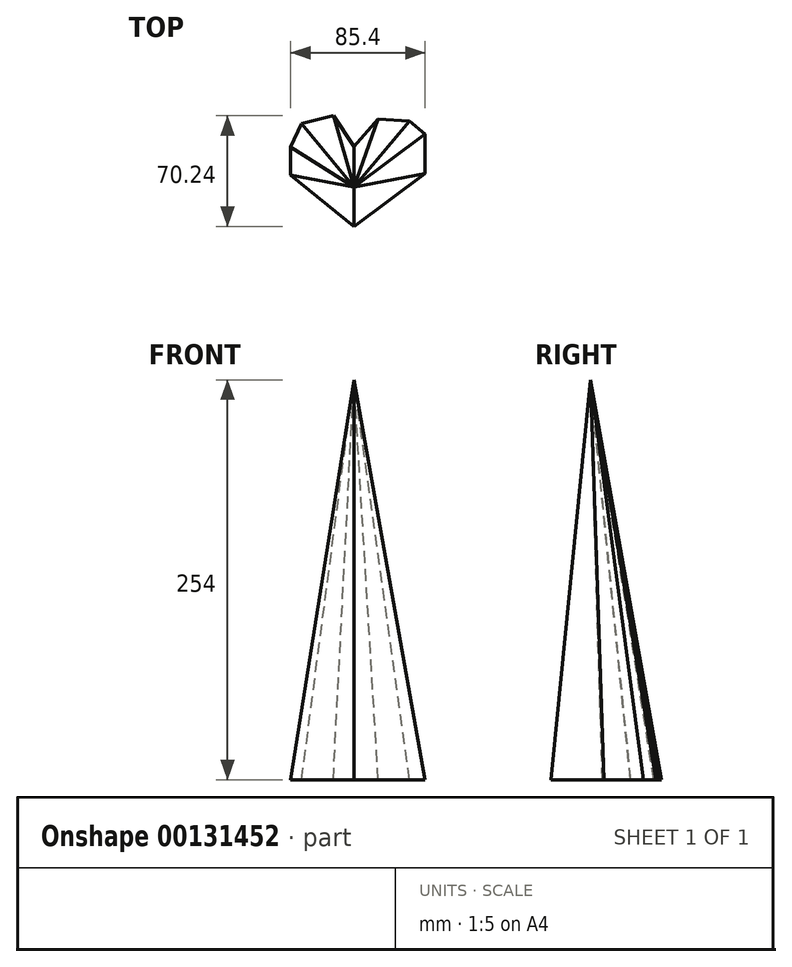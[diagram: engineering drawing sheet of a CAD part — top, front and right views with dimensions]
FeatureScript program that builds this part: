
annotation { "Feature Type Name" : "Feature", "Feature Type Description" : "" }
export const myFeature = defineFeature(function(context is Context, id is Id, definition is map)
    precondition{}
    {
        {
            var Q0;
            Q0=qCreatedBy(makeId("Top.planeOp"),FACE);
            var sketch = newSketch(context, id + "F0", { "sketchPlane" : qUnion([Q0])});
            skLineSegment(sketch, "E0", {"start": v(0, 25.8) * mm, "end": v(15.45, 43.28) * mm});
            skLineSegment(sketch, "E1", {"start": v(15.45, 43.28) * mm, "end": v(35.27, 41.83) * mm});
            skLineSegment(sketch, "E2", {"start": v(35.27, 41.83) * mm, "end": v(45.18, 33.72) * mm});
            skLineSegment(sketch, "E3", {"start": v(45.18, 33.72) * mm, "end": v(45.18, 8.6) * mm});
            skLineSegment(sketch, "E4", {"start": v(45.18, 8.6) * mm, "end": v(0, -24.92) * mm});
            skLineSegment(sketch, "E5", {"start": v(0, -24.92) * mm, "end": v(-40.22, 7.72) * mm});
            skLineSegment(sketch, "E6", {"start": v(-40.22, 7.72) * mm, "end": v(-40.22, 25.5) * mm});
            skLineSegment(sketch, "E7", {"start": v(-40.22, 25.5) * mm, "end": v(-33.23, 40.37) * mm});
            skLineSegment(sketch, "E8", {"start": v(-33.23, 40.37) * mm, "end": v(-13.12, 45.32) * mm});
            skLineSegment(sketch, "E9", {"start": v(-13.12, 45.32) * mm, "end": v(0, 25.8) * mm});
            skSolve(sketch);
        }
        {
            var Q0;
            Q0=qCreatedBy(makeId("Top.planeOp"),FACE);
            cPlane(context, id + "F1", {"entities" : qUnion([Q0]), "cplaneType" : CPlaneType.OFFSET, "offset" : 254 * mm, "width" : 152.4 * mm, "height" : 152.4 * mm});
        }
        {
            var Q0;
            Q0=qCreatedBy(id+"F1.planeOp",FACE);
            var sketch = newSketch(context, id + "F2", { "sketchPlane" : qUnion([Q0])});
            skPoint(sketch, "E10", {"position": v(0, 0) * mm});
            skSolve(sketch);
        }
        {
            var Q0;
            Q0=makeQuery(id+"F0.imprint","IMPRINT",FACE,{"disambiguationData":[TD([[makeQuery(id+"F0.imprint","IMPRINT",EDGE,{"derivedFrom":sQuery(id+"F0.wireOp",EDGE,"E0")}),-1.0]])]});
            var Q1;
            Q1=sQuery(id+"F2.wireOp",VERTEX,"E10");
            loft(context, id + "F3", {"sheetProfilesArray" : [{ "sheetProfileEntities" : qUnion([Q0]) }, { "sheetProfileEntities" : qUnion([Q1]) }]});
        }
    });
